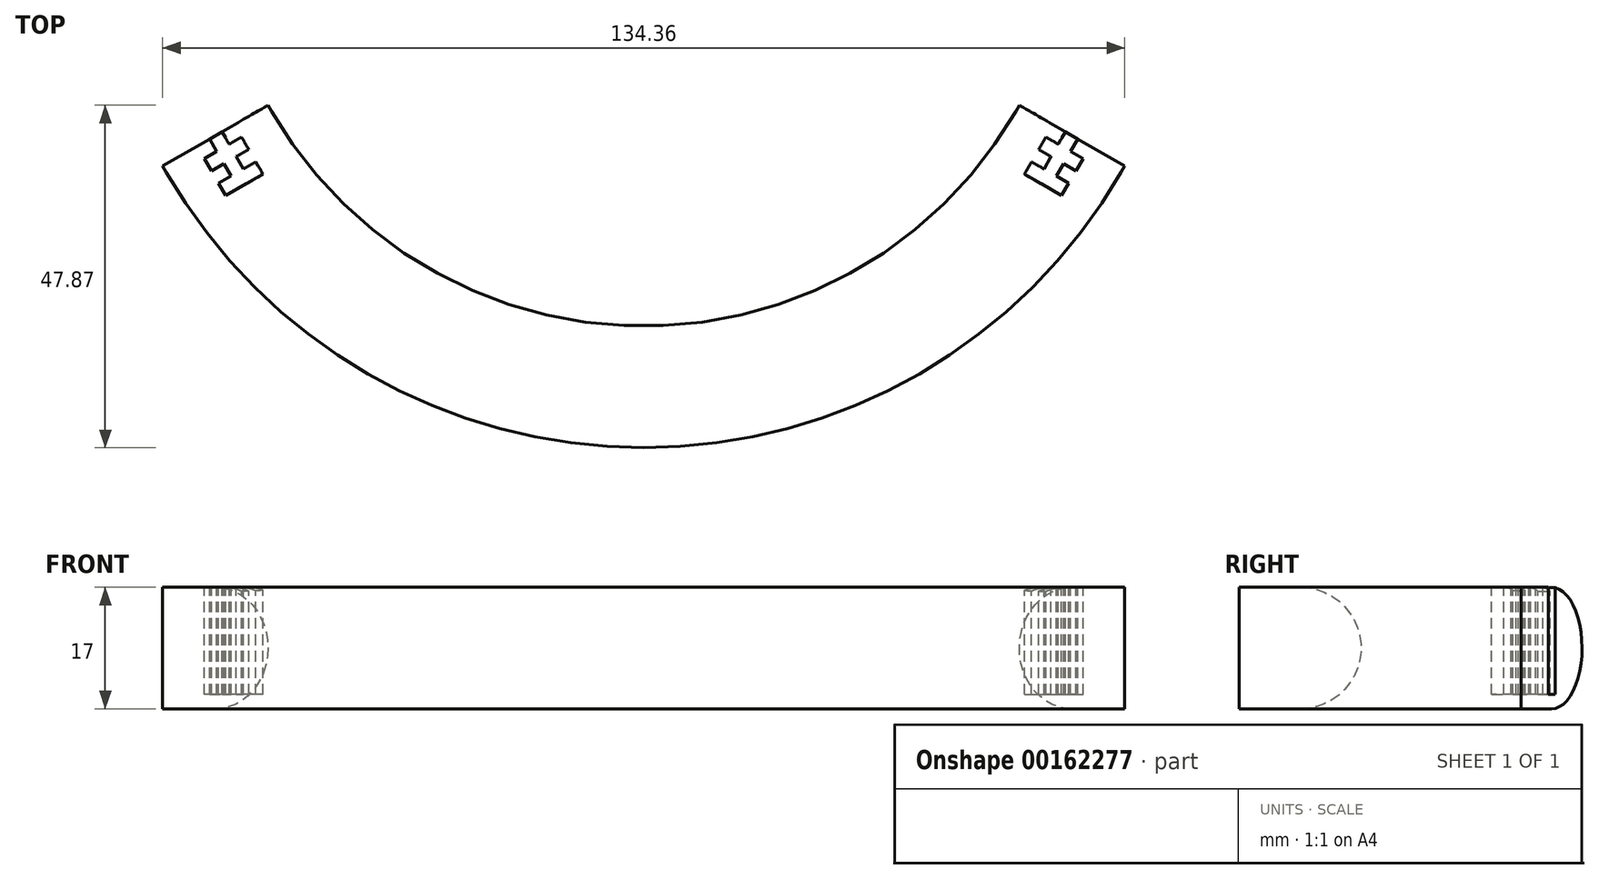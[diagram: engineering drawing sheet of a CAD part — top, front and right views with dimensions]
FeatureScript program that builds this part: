
annotation { "Feature Type Name" : "Feature", "Feature Type Description" : "" }
export const myFeature = defineFeature(function(context is Context, id is Id, definition is map)
    precondition{}
    {
        {
            var Q0;
            Q0=qCreatedBy(makeId("Top.planeOp"),FACE);
            var sketch = newSketch(context, id + "F0", { "sketchPlane" : qUnion([Q0])});
            skArc(sketch, "E0", {"start": v(-51.96, -30) * mm, "mid": v(0, -60) * mm, "end": v(51.96, -30) * mm});
            skArc(sketch, "E1.0", {"start": v(-66.68, -38.5) * mm, "mid": v(0, -77) * mm, "end": v(66.68, -38.5) * mm});
            skLineSegment(sketch, "E2", {"start": v(0, 0) * mm, "end": v(51.96, -30) * mm, "construction": true});
            skLineSegment(sketch, "E3.MirrorCS", {"start": v(0, 0) * mm, "end": v(-51.96, -30) * mm, "construction": true});
            skLineSegment(sketch, "E4.trimOffspring", {"start": v(66.68, -38.5) * mm, "end": v(111.32, -64.27) * mm, "construction": true});
            skLineSegment(sketch, "E5.trimOffspring", {"start": v(-66.68, -38.5) * mm, "end": v(-111.32, -64.27) * mm, "construction": true});
            skPoint(sketch, "E6.end.orphan", {"position": v(-61.84, -1.04) * mm});
            skPoint(sketch, "E7.end.orphan", {"position": v(-74.4, -4.4) * mm});
            skPoint(sketch, "E8.MirrorCS.end.orphan", {"position": v(61.84, -1.04) * mm});
            skPoint(sketch, "E8.MirrorCS.start.orphan", {"position": v(51.96, -30) * mm});
            skPoint(sketch, "E9.MirrorCS.end.orphan", {"position": v(74.4, -4.4) * mm});
            skPoint(sketch, "E10.MirrorCS.start.orphan", {"position": v(66.68, -38.5) * mm});
            skLineSegment(sketch, "E11", {"start": v(-66.68, -38.5) * mm, "end": v(-51.96, -30) * mm});
            skLineSegment(sketch, "E12", {"start": v(51.96, -30) * mm, "end": v(66.68, -38.5) * mm});
            skSolve(sketch);
        }
        {
            var Q0;
            Q0=makeQuery(id+"F0.imprint","IMPRINT",FACE,{"disambiguationData":[TD([[makeQuery(id+"F0.imprint","IMPRINT",EDGE,{"derivedFrom":sQuery(id+"F0.wireOp",EDGE,"E1.0")}),1.0]])]});
            extrude(context, id + "F1", {"entities" : qUnion([Q0]), "depth" : 17 * mm});
        }
        {
            var Q0;
            Q0=makeQuery(id+"F1.opExtrude","CAP_EDGE",EDGE,{"disambiguationData":[OSD([sQuery(id+"F0.wireOp",EDGE,"E0")])],"isStart":false});
            var Q1;
            Q1=makeQuery(id+"F1.opExtrude","CAP_EDGE",EDGE,{"disambiguationData":[OSD([sQuery(id+"F0.wireOp",EDGE,"E0")])],"isStart":true});
            fillet(context, id + "F2", {"entities" : qUnion([Q0, Q1]), "radius" : 8.5 * mm, "tangentPropagation" : true, "allowEdgeOverflow" : false});
        }
        {
            var Q0;
            Q0=makeQuery(id+"F1.opExtrude","SWEPT_FACE",FACE,{"disambiguationData":[OSD([sQuery(id+"F0.wireOp",EDGE,"E11")])]});
            extrude(context, id + "F3", {"entities" : qUnion([Q0]), "operationType" : NewBodyOperationType.ADD, "depth" : 1 * mm});
        }
        {
            var Q0;
            Q0=makeQuery(id+"F1.opExtrude","SWEPT_FACE",FACE,{"disambiguationData":[OSD([sQuery(id+"F0.wireOp",EDGE,"E12")])]});
            extrude(context, id + "F4", {"entities" : qUnion([Q0]), "operationType" : NewBodyOperationType.ADD, "depth" : 1 * mm});
        }
        {
            var Q0;
            {var subQ0=sQuery(id+"F0.wireOp",EDGE,"E11");Q0=makeQuery(id+"F3.boolean.opBoolean","MERGE",FACE,{"derivedFrom":[makeQuery(id+"F1.opExtrude","CAP_FACE",FACE,{"disambiguationData":[OSD([sQuery(id+"F0.wireOp",EDGE,"E0"),sQuery(id+"F0.wireOp",EDGE,"E1.0"),subQ0,sQuery(id+"F0.wireOp",EDGE,"E12")])],"isStart":false}),makeQuery(id+"F3.opExtrude","SWEPT_FACE",FACE,{"disambiguationData":[OSD([subQ0]),TDD([makeQuery(id+"F1.opExtrude","CAP_EDGE",EDGE,{"disambiguationData":[OSD([subQ0])],"isStart":false})])]})]});}
            var sketch = newSketch(context, id + "F5", { "sketchPlane" : qUnion([Q0])});
            skLineSegment(sketch, "E13.bottom", {"start": v(-60.63, -33.85) * mm, "end": v(-56.63, -40.78) * mm});
            skLineSegment(sketch, "E13.top", {"start": v(-58.9, -32.85) * mm, "end": v(-54.9, -39.78) * mm});
            skLineSegment(sketch, "E13.left", {"start": v(-60.63, -33.85) * mm, "end": v(-58.9, -32.85) * mm});
            skLineSegment(sketch, "E13.right", {"start": v(-56.63, -40.78) * mm, "end": v(-54.9, -39.78) * mm});
            skLineSegment(sketch, "E14.bottom", {"start": v(-53.17, -38.78) * mm, "end": v(-54.17, -37.05) * mm});
            skLineSegment(sketch, "E14.top", {"start": v(-58.36, -41.78) * mm, "end": v(-59.36, -40.05) * mm});
            skLineSegment(sketch, "E14.left", {"start": v(-53.17, -38.78) * mm, "end": v(-58.36, -41.78) * mm});
            skLineSegment(sketch, "E14.right", {"start": v(-54.17, -37.05) * mm, "end": v(-59.36, -40.05) * mm});
            skLineSegment(sketch, "E15.bottom", {"start": v(-55.17, -35.31) * mm, "end": v(-56.17, -33.58) * mm});
            skLineSegment(sketch, "E15.top", {"start": v(-60.36, -38.31) * mm, "end": v(-61.36, -36.58) * mm});
            skLineSegment(sketch, "E15.left", {"start": v(-55.17, -35.31) * mm, "end": v(-60.36, -38.31) * mm});
            skLineSegment(sketch, "E15.right", {"start": v(-56.17, -33.58) * mm, "end": v(-61.36, -36.58) * mm});
            skLineSegment(sketch, "E16", {"start": v(-59.82, -33.38) * mm, "end": v(-51.51, -47.78) * mm, "construction": true});
            skLineSegment(sketch, "E17", {"start": v(-59.76, -33.35) * mm, "end": v(-55.76, -40.28) * mm});
            skLineSegment(sketch, "E18.MirrorCS", {"start": v(60.63, -33.85) * mm, "end": v(58.9, -32.85) * mm});
            skLineSegment(sketch, "E19.MirrorCS", {"start": v(56.63, -40.78) * mm, "end": v(54.9, -39.78) * mm});
            skLineSegment(sketch, "E20.MirrorCS", {"start": v(60.36, -38.31) * mm, "end": v(61.36, -36.58) * mm});
            skLineSegment(sketch, "E21.MirrorCS", {"start": v(53.17, -38.78) * mm, "end": v(54.17, -37.05) * mm});
            skLineSegment(sketch, "E22.MirrorCS", {"start": v(55.17, -35.31) * mm, "end": v(56.17, -33.58) * mm});
            skLineSegment(sketch, "E23.MirrorCS", {"start": v(58.9, -32.85) * mm, "end": v(54.9, -39.78) * mm});
            skLineSegment(sketch, "E24.MirrorCS", {"start": v(60.63, -33.85) * mm, "end": v(56.63, -40.78) * mm});
            skLineSegment(sketch, "E25.MirrorCS", {"start": v(54.17, -37.05) * mm, "end": v(59.36, -40.05) * mm});
            skLineSegment(sketch, "E26.MirrorCS", {"start": v(59.76, -33.35) * mm, "end": v(55.76, -40.28) * mm});
            skLineSegment(sketch, "E27.MirrorCS", {"start": v(59.82, -33.38) * mm, "end": v(51.51, -47.78) * mm, "construction": true});
            skLineSegment(sketch, "E28.MirrorCS", {"start": v(53.17, -38.78) * mm, "end": v(58.36, -41.78) * mm});
            skLineSegment(sketch, "E29.MirrorCS", {"start": v(55.17, -35.31) * mm, "end": v(60.36, -38.31) * mm});
            skLineSegment(sketch, "E30.MirrorCS", {"start": v(58.36, -41.78) * mm, "end": v(59.36, -40.05) * mm});
            skLineSegment(sketch, "E31.MirrorCS", {"start": v(56.17, -33.58) * mm, "end": v(61.36, -36.58) * mm});
            skSolve(sketch);
        }
        {
            var Q0;
            Q0 = qSketchRegion(id + "F5", true);
            extrude(context, id + "F6", {"entities" : qUnion([Q0]), "operationType" : NewBodyOperationType.ADD, "oppositeDirection" : true, "depth" : 8.68 * mm});
        }
        {
            var Q0;
            Q0 = qSketchRegion(id + "F5", true);
            var Q1;
            Q1=makeQuery(id+"F2.opFillet","BLEND_FACE",FACE,{"disambiguationData":[OSD([sQuery(id+"F0.wireOp",EDGE,"E0")])]});
            extrude(context, id + "F7", {"entities" : qUnion([Q0]), "operationType" : NewBodyOperationType.REMOVE, "oppositeDirection" : true, "endBoundEntityFace" : qUnion([Q1]), "depth" : 15 * mm});
        }
    });
